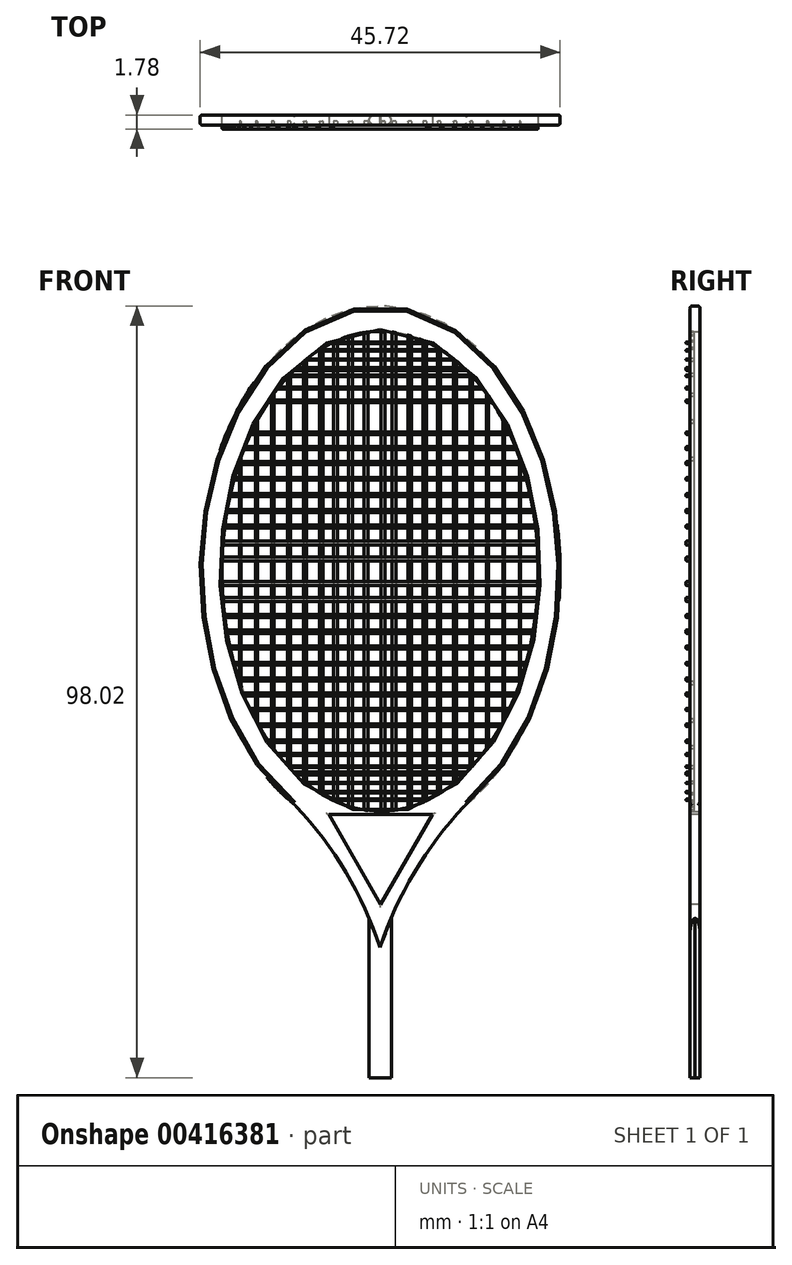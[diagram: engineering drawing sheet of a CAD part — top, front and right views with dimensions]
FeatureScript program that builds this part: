
annotation { "Feature Type Name" : "Feature", "Feature Type Description" : "" }
export const myFeature = defineFeature(function(context is Context, id is Id, definition is map)
    precondition{}
    {
        {
            var Q0;
            Q0=qCreatedBy(makeId("Front.planeOp"),FACE);
            var sketch = newSketch(context, id + "F0", { "sketchPlane" : qUnion([Q0])});
            skEllipse(sketch, "E0", {"center": v(0, 0) * mm, "majorRadius": 33.69 * mm, "minorRadius": 22.86 * mm, "majorAxis": v(0, 1)});
            skEllipse(sketch, "E1", {"center": v(0, 0) * mm, "majorRadius": 30.48 * mm, "minorRadius": 20.09 * mm, "majorAxis": v(0, 1)});
            skArc(sketch, "E2", {"start": v(13.9, -26.75) * mm, "mid": v(5.55, -36.34) * mm, "end": v(0, -47.78) * mm});
            skArc(sketch, "E3.MirrorCS", {"start": v(-13.9, -26.75) * mm, "mid": v(-5.55, -36.34) * mm, "end": v(0, -47.78) * mm});
            skSolve(sketch);
        }
        {
            var Q0;
            Q0 = qSketchRegion(id + "F0", true);
            extrude(context, id + "F1", {"entities" : qUnion([Q0]), "depth" : 1.27 * mm});
        }
        {
            var Q0;
            Q0=makeQuery(id+"F1.opExtrude","CAP_FACE",FACE,{"disambiguationData":[OSD([sQuery(id+"F0.wireOp",EDGE,"E0"),sQuery(id+"F0.wireOp",EDGE,"E1"),sQuery(id+"F0.wireOp",EDGE,"E2"),sQuery(id+"F0.wireOp",EDGE,"E3.MirrorCS")])],"isStart":false});
            var sketch = newSketch(context, id + "F2", { "sketchPlane" : qUnion([Q0])});
            skLineSegment(sketch, "E4", {"start": v(-6.5, -30.9) * mm, "end": v(6.64, -30.9) * mm});
            skLineSegment(sketch, "E5", {"start": v(6.64, -30.9) * mm, "end": v(0.07, -42.3) * mm});
            skLineSegment(sketch, "E6", {"start": v(0.07, -42.3) * mm, "end": v(-6.5, -30.9) * mm});
            skSolve(sketch);
        }
        {
            var Q0;
            Q0=makeQuery(id+"F2.imprint","IMPRINT",FACE,{"disambiguationData":[TD([[makeQuery(id+"F2.imprint","IMPRINT",EDGE,{"derivedFrom":sQuery(id+"F2.wireOp",EDGE,"E4")}),-1.0]])]});
            extrude(context, id + "F3", {"entities" : qUnion([Q0]), "operationType" : NewBodyOperationType.REMOVE, "oppositeDirection" : true, "depth" : 25.4 * mm});
        }
        {
            var Q0;
            Q0=qCreatedBy(makeId("Front.planeOp"),FACE);
            var sketch = newSketch(context, id + "F4", { "sketchPlane" : qUnion([Q0])});
            skLineSegment(sketch, "E7", {"start": v(1.42, -44.01) * mm, "end": v(1.42, -64.33) * mm});
            skLineSegment(sketch, "E8", {"start": v(1.42, -64.33) * mm, "end": v(-1.43, -64.33) * mm});
            skLineSegment(sketch, "E9", {"start": v(-1.43, -64.33) * mm, "end": v(-1.43, -44.01) * mm});
            skLineSegment(sketch, "E10", {"start": v(1.42, -44.01) * mm, "end": v(0, -47.74) * mm});
            skLineSegment(sketch, "E11", {"start": v(0, -47.74) * mm, "end": v(-1.43, -44.01) * mm});
            skSolve(sketch);
        }
        {
            var Q0;
            Q0 = qSketchRegion(id + "F4", true);
            extrude(context, id + "F5", {"entities" : qUnion([Q0]), "depth" : 1.27 * mm});
        }
        {
            var Q0;
            Q0=makeQuery(id+"F1.opExtrude","CAP_FACE",FACE,{"disambiguationData":[OSD([sQuery(id+"F0.wireOp",EDGE,"E0"),sQuery(id+"F0.wireOp",EDGE,"E1"),sQuery(id+"F0.wireOp",EDGE,"E2"),sQuery(id+"F0.wireOp",EDGE,"E3.MirrorCS")])],"isStart":false});
            var sketch = newSketch(context, id + "F6", { "sketchPlane" : qUnion([Q0])});
            skLineSegment(sketch, "E12", {"start": v(-15.82, 18.79) * mm, "end": v(-15.82, -18.79) * mm});
            skLineSegment(sketch, "E13", {"start": v(-13.79, 22.17) * mm, "end": v(-13.79, -22.17) * mm});
            skLineSegment(sketch, "E14", {"start": v(-11.75, 24.72) * mm, "end": v(-11.75, -24.72) * mm});
            skLineSegment(sketch, "E15", {"start": v(-9.72, 26.67) * mm, "end": v(-9.72, -26.67) * mm});
            skLineSegment(sketch, "E16", {"start": v(-7.69, 28.16) * mm, "end": v(-7.69, -28.16) * mm});
            skLineSegment(sketch, "E17.MirrorCS", {"start": v(7.69, 28.16) * mm, "end": v(7.69, -28.16) * mm});
            skLineSegment(sketch, "E18.MirrorCS", {"start": v(9.72, 26.67) * mm, "end": v(9.72, -26.67) * mm});
            skLineSegment(sketch, "E19.MirrorCS", {"start": v(11.75, 24.72) * mm, "end": v(11.75, -24.72) * mm});
            skLineSegment(sketch, "E20.MirrorCS", {"start": v(13.79, 22.17) * mm, "end": v(13.79, -22.17) * mm});
            skLineSegment(sketch, "E21.MirrorCS", {"start": v(15.82, 18.79) * mm, "end": v(15.82, -18.79) * mm});
            skLineSegment(sketch, "E22", {"start": v(-17.85, 13.98) * mm, "end": v(-17.85, -13.98) * mm});
            skLineSegment(sketch, "E23.MirrorCS", {"start": v(17.85, 13.98) * mm, "end": v(17.85, -13.98) * mm});
            skLineSegment(sketch, "E24", {"start": v(-5.9, 29.13) * mm, "end": v(-5.9, -29.13) * mm});
            skLineSegment(sketch, "E25", {"start": v(-4.01, 29.87) * mm, "end": v(-4.01, -29.87) * mm});
            skLineSegment(sketch, "E26", {"start": v(-2.03, 30.32) * mm, "end": v(-2.03, -30.32) * mm});
            skLineSegment(sketch, "E27.MirrorCS", {"start": v(2.03, 30.32) * mm, "end": v(2.03, -30.32) * mm});
            skLineSegment(sketch, "E28.MirrorCS", {"start": v(4.01, 29.87) * mm, "end": v(4.01, -29.87) * mm});
            skLineSegment(sketch, "E29.MirrorCS", {"start": v(5.9, 29.13) * mm, "end": v(5.9, -29.13) * mm});
            skLineSegment(sketch, "E30", {"start": v(-17.68, 14.46) * mm, "end": v(-17.68, -14.46) * mm});
            skLineSegment(sketch, "E31", {"start": v(-15.58, 19.24) * mm, "end": v(-15.58, -19.24) * mm});
            skLineSegment(sketch, "E32", {"start": v(-13.5, 22.58) * mm, "end": v(-13.5, -22.58) * mm});
            skLineSegment(sketch, "E33", {"start": v(-11.4, 25.09) * mm, "end": v(-11.4, -25.09) * mm});
            skLineSegment(sketch, "E34", {"start": v(-9.33, 27) * mm, "end": v(-9.33, -27) * mm});
            skLineSegment(sketch, "E35", {"start": v(-7.26, 28.42) * mm, "end": v(-7.26, -28.42) * mm});
            skLineSegment(sketch, "E36", {"start": v(-5.44, 29.34) * mm, "end": v(-5.44, -29.34) * mm});
            skLineSegment(sketch, "E37", {"start": v(-3.52, 30) * mm, "end": v(-3.52, -30) * mm});
            skLineSegment(sketch, "E38", {"start": v(-1.53, 30.4) * mm, "end": v(-1.53, -30.4) * mm});
            skLineSegment(sketch, "E39.MirrorCS", {"start": v(17.68, 14.46) * mm, "end": v(17.68, -14.46) * mm});
            skLineSegment(sketch, "E40.MirrorCS", {"start": v(15.58, 19.24) * mm, "end": v(15.58, -19.24) * mm});
            skLineSegment(sketch, "E41.MirrorCS", {"start": v(13.5, 22.58) * mm, "end": v(13.5, -22.58) * mm});
            skLineSegment(sketch, "E42.MirrorCS", {"start": v(11.4, 25.09) * mm, "end": v(11.4, -25.09) * mm});
            skLineSegment(sketch, "E43.MirrorCS", {"start": v(9.33, 27) * mm, "end": v(9.33, -27) * mm});
            skLineSegment(sketch, "E44.MirrorCS", {"start": v(7.26, 28.42) * mm, "end": v(7.26, -28.42) * mm});
            skLineSegment(sketch, "E45.MirrorCS", {"start": v(5.44, 29.34) * mm, "end": v(5.44, -29.34) * mm});
            skLineSegment(sketch, "E46.MirrorCS", {"start": v(3.52, 30) * mm, "end": v(3.52, -30) * mm});
            skLineSegment(sketch, "E47.MirrorCS", {"start": v(1.53, 30.4) * mm, "end": v(1.53, -30.4) * mm});
            skLineSegment(sketch, "E48", {"start": v(0.1, 30.48) * mm, "end": v(0.1, -30.48) * mm});
            skLineSegment(sketch, "E49", {"start": v(0.61, 30.47) * mm, "end": v(0.61, -30.47) * mm});
            skSolve(sketch);
        }
        {
            var Q0;
            Q0=makeQuery(id+"F6.imprint","IMPRINT",FACE,{"disambiguationData":[TD([[makeQuery(id+"F6.imprint","IMPRINT",EDGE,{"derivedFrom":makeQuery(id+"F1.opExtrude","CAP_EDGE",EDGE,{"disambiguationData":[OSD([sQuery(id+"F0.wireOp",EDGE,"E0")])],"isStart":false})}),1.0]])]});
            var sketch = newSketch(context, id + "F7", { "sketchPlane" : qUnion([Q0])});
            skLineSegment(sketch, "E50", {"start": v(-5.9, 29.13) * mm, "end": v(5.9, 29.13) * mm});
            skLineSegment(sketch, "E51", {"start": v(-7.69, 28.16) * mm, "end": v(7.69, 28.16) * mm});
            skLineSegment(sketch, "E52", {"start": v(-9.35, 26.98) * mm, "end": v(9.35, 26.98) * mm});
            skLineSegment(sketch, "E53", {"start": v(-11.54, 24.95) * mm, "end": v(11.54, 24.95) * mm});
            skLineSegment(sketch, "E54", {"start": v(-12.87, 23.4) * mm, "end": v(12.87, 23.4) * mm});
            skLineSegment(sketch, "E55", {"start": v(-14.06, 21.77) * mm, "end": v(14.06, 21.77) * mm});
            skLineSegment(sketch, "E56", {"start": v(-15.3, 19.73) * mm, "end": v(15.3, 19.73) * mm});
            skLineSegment(sketch, "E57", {"start": v(15.3, 19.73) * mm, "end": v(-15.3, 19.73) * mm});
            skLineSegment(sketch, "E58", {"start": v(-16.35, 17.7) * mm, "end": v(16.35, 17.7) * mm});
            skLineSegment(sketch, "E59", {"start": v(-17.16, 15.84) * mm, "end": v(17.16, 15.84) * mm});
            skLineSegment(sketch, "E60", {"start": v(-17.87, 13.93) * mm, "end": v(17.87, 13.93) * mm});
            skLineSegment(sketch, "E61", {"start": v(-18.5, 11.9) * mm, "end": v(18.5, 11.9) * mm});
            skLineSegment(sketch, "E62", {"start": v(-19, 9.87) * mm, "end": v(19, 9.87) * mm});
            skLineSegment(sketch, "E63", {"start": v(-19.4, 7.88) * mm, "end": v(19.4, 7.88) * mm});
            skLineSegment(sketch, "E64", {"start": v(-19.71, 5.87) * mm, "end": v(19.71, 5.87) * mm});
            skLineSegment(sketch, "E65", {"start": v(-20.05, 3.83) * mm, "end": v(19.93, 3.83) * mm});
            skLineSegment(sketch, "E66", {"start": v(-20.05, 1.8) * mm, "end": v(20.05, 1.8) * mm});
            skLineSegment(sketch, "E67", {"start": v(-20.99, 0) * mm, "end": v(20.09, 0) * mm});
            skLineSegment(sketch, "E68.MirrorCS", {"start": v(-20.05, -1.8) * mm, "end": v(20.05, -1.8) * mm});
            skLineSegment(sketch, "E69.MirrorCS", {"start": v(-20.05, -3.83) * mm, "end": v(19.93, -3.83) * mm});
            skLineSegment(sketch, "E70.MirrorCS", {"start": v(-19.71, -5.87) * mm, "end": v(19.71, -5.87) * mm});
            skLineSegment(sketch, "E71.MirrorCS", {"start": v(-19.4, -7.88) * mm, "end": v(19.4, -7.88) * mm});
            skLineSegment(sketch, "E72.MirrorCS", {"start": v(-5.9, -29.13) * mm, "end": v(5.9, -29.13) * mm});
            skLineSegment(sketch, "E73.MirrorCS", {"start": v(-7.69, -28.16) * mm, "end": v(7.69, -28.16) * mm});
            skLineSegment(sketch, "E74.MirrorCS", {"start": v(-9.35, -26.98) * mm, "end": v(9.35, -26.98) * mm});
            skLineSegment(sketch, "E75.MirrorCS", {"start": v(-11.54, -24.95) * mm, "end": v(11.54, -24.95) * mm});
            skLineSegment(sketch, "E76.MirrorCS", {"start": v(-12.87, -23.4) * mm, "end": v(12.87, -23.4) * mm});
            skLineSegment(sketch, "E77.MirrorCS", {"start": v(-14.06, -21.77) * mm, "end": v(14.06, -21.77) * mm});
            skLineSegment(sketch, "E78.MirrorCS", {"start": v(15.3, -19.73) * mm, "end": v(-15.3, -19.73) * mm});
            skLineSegment(sketch, "E79.MirrorCS", {"start": v(-16.35, -17.7) * mm, "end": v(16.35, -17.7) * mm});
            skLineSegment(sketch, "E80.MirrorCS", {"start": v(-17.16, -15.84) * mm, "end": v(17.16, -15.84) * mm});
            skLineSegment(sketch, "E81.MirrorCS", {"start": v(-17.87, -13.93) * mm, "end": v(17.87, -13.93) * mm});
            skLineSegment(sketch, "E82.MirrorCS", {"start": v(-18.5, -11.9) * mm, "end": v(18.5, -11.9) * mm});
            skLineSegment(sketch, "E83.MirrorCS", {"start": v(-19, -9.87) * mm, "end": v(19, -9.87) * mm});
            skLineSegment(sketch, "E84", {"start": v(-6.37, 28.93) * mm, "end": v(7.07, 28.93) * mm});
            skLineSegment(sketch, "E85", {"start": v(-8.16, 27.96) * mm, "end": v(8.72, 27.96) * mm});
            skLineSegment(sketch, "E86", {"start": v(-9.83, 26.82) * mm, "end": v(10.64, 26.82) * mm});
            skLineSegment(sketch, "E87", {"start": v(-11.99, 24.7) * mm, "end": v(12.2, 24.7) * mm});
            skLineSegment(sketch, "E88", {"start": v(-13.3, 23.14) * mm, "end": v(13.48, 23.14) * mm});
            skLineSegment(sketch, "E89", {"start": v(-14.45, 21.44) * mm, "end": v(14.63, 21.44) * mm});
            skLineSegment(sketch, "E90", {"start": v(-15.67, 19.37) * mm, "end": v(15.85, 19.37) * mm});
            skLineSegment(sketch, "E91", {"start": v(-17.16, 17.4) * mm, "end": v(16.88, 17.4) * mm});
            skLineSegment(sketch, "E92", {"start": v(-17.47, 15.44) * mm, "end": v(17.92, 15.44) * mm});
            skLineSegment(sketch, "E93", {"start": v(-18.2, 13.54) * mm, "end": v(18.63, 13.54) * mm});
            skLineSegment(sketch, "E94", {"start": v(-18.88, 11.57) * mm, "end": v(19.66, 11.57) * mm});
            skLineSegment(sketch, "E95", {"start": v(-19.35, 9.5) * mm, "end": v(19.83, 9.5) * mm});
            skLineSegment(sketch, "E96", {"start": v(-19.66, 7.44) * mm, "end": v(19.96, 7.44) * mm});
            skLineSegment(sketch, "E97", {"start": v(-20.08, 5.51) * mm, "end": v(19.86, 5.51) * mm});
            skLineSegment(sketch, "E98", {"start": v(-20.08, 3.33) * mm, "end": v(20.38, 3.33) * mm});
            skLineSegment(sketch, "E99", {"start": v(-20.2, 1.32) * mm, "end": v(20.18, 1.32) * mm});
            skLineSegment(sketch, "E100.MirrorCS", {"start": v(-20.2, -1.32) * mm, "end": v(20.18, -1.32) * mm});
            skLineSegment(sketch, "E101.MirrorCS", {"start": v(-20.08, -3.33) * mm, "end": v(20.38, -3.33) * mm});
            skLineSegment(sketch, "E102.MirrorCS", {"start": v(-20.08, -5.51) * mm, "end": v(19.86, -5.51) * mm});
            skLineSegment(sketch, "E103.MirrorCS", {"start": v(-19.66, -7.44) * mm, "end": v(19.96, -7.44) * mm});
            skLineSegment(sketch, "E104.MirrorCS", {"start": v(-19.35, -9.5) * mm, "end": v(19.83, -9.5) * mm});
            skLineSegment(sketch, "E105.MirrorCS", {"start": v(-18.88, -11.57) * mm, "end": v(19.66, -11.57) * mm});
            skLineSegment(sketch, "E106.MirrorCS", {"start": v(-18.2, -13.54) * mm, "end": v(18.63, -13.54) * mm});
            skLineSegment(sketch, "E107.MirrorCS", {"start": v(-17.47, -15.44) * mm, "end": v(17.92, -15.44) * mm});
            skLineSegment(sketch, "E108.MirrorCS", {"start": v(-17.16, -17.4) * mm, "end": v(16.88, -17.4) * mm});
            skLineSegment(sketch, "E109.MirrorCS", {"start": v(-15.67, -19.37) * mm, "end": v(15.85, -19.37) * mm});
            skLineSegment(sketch, "E110.MirrorCS", {"start": v(-14.45, -21.44) * mm, "end": v(14.63, -21.44) * mm});
            skLineSegment(sketch, "E111.MirrorCS", {"start": v(-13.3, -23.14) * mm, "end": v(13.48, -23.14) * mm});
            skLineSegment(sketch, "E112.MirrorCS", {"start": v(-11.99, -24.7) * mm, "end": v(12.2, -24.7) * mm});
            skLineSegment(sketch, "E113.MirrorCS", {"start": v(-9.83, -26.82) * mm, "end": v(10.64, -26.82) * mm});
            skLineSegment(sketch, "E114.MirrorCS", {"start": v(-8.16, -27.96) * mm, "end": v(8.72, -27.96) * mm});
            skLineSegment(sketch, "E115.MirrorCS", {"start": v(-6.37, -28.93) * mm, "end": v(7.07, -28.93) * mm});
            skLineSegment(sketch, "E116", {"start": v(-11.06, 25.88) * mm, "end": v(10.6, 25.88) * mm});
            skLineSegment(sketch, "E117", {"start": v(-11.42, 25.52) * mm, "end": v(10.98, 25.52) * mm});
            skLineSegment(sketch, "E118.MirrorCS", {"start": v(-11.06, -25.88) * mm, "end": v(10.6, -25.88) * mm});
            skLineSegment(sketch, "E119.MirrorCS", {"start": v(-11.42, -25.52) * mm, "end": v(10.98, -25.52) * mm});
            skSolve(sketch);
        }
        {
            var Q0;
            Q0=makeQuery(id+"F5.opExtrude","CAP_EDGE",EDGE,{"disambiguationData":[OSD([sQuery(id+"F4.wireOp",EDGE,"E7")])],"isStart":true});
            var Q1;
            Q1=makeQuery(id+"F5.opExtrude","CAP_EDGE",EDGE,{"disambiguationData":[OSD([sQuery(id+"F4.wireOp",EDGE,"E7")])],"isStart":false});
            var Q2;
            Q2=makeQuery(id+"F5.opExtrude","CAP_EDGE",EDGE,{"disambiguationData":[OSD([sQuery(id+"F4.wireOp",EDGE,"E9")])],"isStart":true});
            var Q3;
            Q3=makeQuery(id+"F5.opExtrude","CAP_EDGE",EDGE,{"disambiguationData":[OSD([sQuery(id+"F4.wireOp",EDGE,"E9")])],"isStart":false});
            fillet(context, id + "F8", {"entities" : qUnion([Q0, Q1, Q2, Q3]), "radius" : 0.76 * mm, "tangentPropagation" : true, "allowEdgeOverflow" : false});
        }
        {
            var Q0;
            {var subQ0=sQuery(id+"F6.wireOp",EDGE,"E22");Q0=makeQuery(id+"F6.imprint","IMPRINT",FACE,{"disambiguationData":[TD([[makeQuery(id+"F6.imprint","IMPRINT",EDGE,{"derivedFrom":subQ0}),1.0]])]});}
            var Q1;
            {var subQ0=sQuery(id+"F6.wireOp",EDGE,"E12");Q1=makeQuery(id+"F6.imprint","IMPRINT",FACE,{"disambiguationData":[TD([[makeQuery(id+"F6.imprint","IMPRINT",EDGE,{"derivedFrom":subQ0}),1.0]])]});}
            var Q2;
            {var subQ0=sQuery(id+"F6.wireOp",EDGE,"E13");Q2=makeQuery(id+"F6.imprint","IMPRINT",FACE,{"disambiguationData":[TD([[makeQuery(id+"F6.imprint","IMPRINT",EDGE,{"derivedFrom":subQ0}),1.0]])]});}
            var Q3;
            {var subQ0=sQuery(id+"F6.wireOp",EDGE,"E14");Q3=makeQuery(id+"F6.imprint","IMPRINT",FACE,{"disambiguationData":[TD([[makeQuery(id+"F6.imprint","IMPRINT",EDGE,{"derivedFrom":subQ0}),1.0]])]});}
            var Q4;
            {var subQ0=sQuery(id+"F6.wireOp",EDGE,"E16");Q4=makeQuery(id+"F6.imprint","IMPRINT",FACE,{"disambiguationData":[TD([[makeQuery(id+"F6.imprint","IMPRINT",EDGE,{"derivedFrom":subQ0}),1.0]])]});}
            var Q5;
            {var subQ0=sQuery(id+"F6.wireOp",EDGE,"E25");Q5=makeQuery(id+"F6.imprint","IMPRINT",FACE,{"disambiguationData":[TD([[makeQuery(id+"F6.imprint","IMPRINT",EDGE,{"derivedFrom":subQ0}),1.0]])]});}
            var Q6;
            {var subQ0=sQuery(id+"F6.wireOp",EDGE,"E24");Q6=makeQuery(id+"F6.imprint","IMPRINT",FACE,{"disambiguationData":[TD([[makeQuery(id+"F6.imprint","IMPRINT",EDGE,{"derivedFrom":subQ0}),1.0]])]});}
            var Q7;
            {var subQ0=sQuery(id+"F6.wireOp",EDGE,"E15");Q7=makeQuery(id+"F6.imprint","IMPRINT",FACE,{"disambiguationData":[TD([[makeQuery(id+"F6.imprint","IMPRINT",EDGE,{"derivedFrom":subQ0}),1.0]])]});}
            var Q8;
            {var subQ0=sQuery(id+"F6.wireOp",EDGE,"E26");Q8=makeQuery(id+"F6.imprint","IMPRINT",FACE,{"disambiguationData":[TD([[makeQuery(id+"F6.imprint","IMPRINT",EDGE,{"derivedFrom":subQ0}),1.0]])]});}
            var Q9;
            {var subQ0=sQuery(id+"F6.wireOp",EDGE,"E27.MirrorCS");Q9=makeQuery(id+"F6.imprint","IMPRINT",FACE,{"disambiguationData":[TD([[makeQuery(id+"F6.imprint","IMPRINT",EDGE,{"derivedFrom":subQ0}),-1.0]])]});}
            var Q10;
            {var subQ0=sQuery(id+"F6.wireOp",EDGE,"E23.MirrorCS");Q10=makeQuery(id+"F6.imprint","IMPRINT",FACE,{"disambiguationData":[TD([[makeQuery(id+"F6.imprint","IMPRINT",EDGE,{"derivedFrom":subQ0}),-1.0]])]});}
            var Q11;
            {var subQ0=sQuery(id+"F6.wireOp",EDGE,"E18.MirrorCS");Q11=makeQuery(id+"F6.imprint","IMPRINT",FACE,{"disambiguationData":[TD([[makeQuery(id+"F6.imprint","IMPRINT",EDGE,{"derivedFrom":subQ0}),-1.0]])]});}
            var Q12;
            {var subQ0=sQuery(id+"F6.wireOp",EDGE,"E29.MirrorCS");Q12=makeQuery(id+"F6.imprint","IMPRINT",FACE,{"disambiguationData":[TD([[makeQuery(id+"F6.imprint","IMPRINT",EDGE,{"derivedFrom":subQ0}),-1.0]])]});}
            var Q13;
            {var subQ0=sQuery(id+"F6.wireOp",EDGE,"E17.MirrorCS");Q13=makeQuery(id+"F6.imprint","IMPRINT",FACE,{"disambiguationData":[TD([[makeQuery(id+"F6.imprint","IMPRINT",EDGE,{"derivedFrom":subQ0}),-1.0]])]});}
            var Q14;
            {var subQ0=sQuery(id+"F6.wireOp",EDGE,"E19.MirrorCS");Q14=makeQuery(id+"F6.imprint","IMPRINT",FACE,{"disambiguationData":[TD([[makeQuery(id+"F6.imprint","IMPRINT",EDGE,{"derivedFrom":subQ0}),-1.0]])]});}
            var Q15;
            {var subQ0=sQuery(id+"F6.wireOp",EDGE,"E20.MirrorCS");Q15=makeQuery(id+"F6.imprint","IMPRINT",FACE,{"disambiguationData":[TD([[makeQuery(id+"F6.imprint","IMPRINT",EDGE,{"derivedFrom":subQ0}),-1.0]])]});}
            var Q16;
            {var subQ0=sQuery(id+"F6.wireOp",EDGE,"E21.MirrorCS");Q16=makeQuery(id+"F6.imprint","IMPRINT",FACE,{"disambiguationData":[TD([[makeQuery(id+"F6.imprint","IMPRINT",EDGE,{"derivedFrom":subQ0}),-1.0]])]});}
            var Q17;
            {var subQ0=sQuery(id+"F6.wireOp",EDGE,"E28.MirrorCS");Q17=makeQuery(id+"F6.imprint","IMPRINT",FACE,{"disambiguationData":[TD([[makeQuery(id+"F6.imprint","IMPRINT",EDGE,{"derivedFrom":subQ0}),-1.0]])]});}
            var Q18;
            {var subQ0=sQuery(id+"F6.wireOp",EDGE,"E48");Q18=makeQuery(id+"F6.imprint","IMPRINT",FACE,{"disambiguationData":[TD([[makeQuery(id+"F6.imprint","IMPRINT",EDGE,{"derivedFrom":subQ0}),1.0]])]});}
            extrude(context, id + "F9", {"entities" : qUnion([Q0, Q1, Q2, Q3, Q4, Q5, Q6, Q7, Q8, Q9, Q10, Q11, Q12, Q13, Q14, Q15, Q16, Q17, Q18]), "oppositeDirection" : true, "depth" : 0.5 * mm});
        }
        {
            var Q0;
            {var subQ0=sQuery(id+"F7.wireOp",EDGE,"E59");Q0=makeQuery(id+"F7.imprint","IMPRINT",FACE,{"disambiguationData":[TD([[makeQuery(id+"F7.imprint","IMPRINT",EDGE,{"derivedFrom":subQ0}),-1.0]])]});}
            var Q1;
            {var subQ0=sQuery(id+"F7.wireOp",EDGE,"E58");Q1=makeQuery(id+"F7.imprint","IMPRINT",FACE,{"disambiguationData":[TD([[makeQuery(id+"F7.imprint","IMPRINT",EDGE,{"derivedFrom":subQ0}),-1.0]])]});}
            var Q2;
            {var subQ0=sQuery(id+"F7.wireOp",EDGE,"E60");Q2=makeQuery(id+"F7.imprint","IMPRINT",FACE,{"disambiguationData":[TD([[makeQuery(id+"F7.imprint","IMPRINT",EDGE,{"derivedFrom":subQ0}),-1.0]])]});}
            var Q3;
            {var subQ0=sQuery(id+"F7.wireOp",EDGE,"E61");Q3=makeQuery(id+"F7.imprint","IMPRINT",FACE,{"disambiguationData":[TD([[makeQuery(id+"F7.imprint","IMPRINT",EDGE,{"derivedFrom":subQ0}),-1.0]])]});}
            var Q4;
            {var subQ0=sQuery(id+"F7.wireOp",EDGE,"E79.MirrorCS");Q4=makeQuery(id+"F7.imprint","IMPRINT",FACE,{"disambiguationData":[TD([[makeQuery(id+"F7.imprint","IMPRINT",EDGE,{"derivedFrom":subQ0}),1.0]])]});}
            var Q5;
            {var subQ0=sQuery(id+"F7.wireOp",EDGE,"E80.MirrorCS");Q5=makeQuery(id+"F7.imprint","IMPRINT",FACE,{"disambiguationData":[TD([[makeQuery(id+"F7.imprint","IMPRINT",EDGE,{"derivedFrom":subQ0}),1.0]])]});}
            var Q6;
            {var subQ0=sQuery(id+"F7.wireOp",EDGE,"E81.MirrorCS");Q6=makeQuery(id+"F7.imprint","IMPRINT",FACE,{"disambiguationData":[TD([[makeQuery(id+"F7.imprint","IMPRINT",EDGE,{"derivedFrom":subQ0}),1.0]])]});}
            var Q7;
            {var subQ0=sQuery(id+"F7.wireOp",EDGE,"E82.MirrorCS");Q7=makeQuery(id+"F7.imprint","IMPRINT",FACE,{"disambiguationData":[TD([[makeQuery(id+"F7.imprint","IMPRINT",EDGE,{"derivedFrom":subQ0}),1.0]])]});}
            var Q8;
            {var subQ0=sQuery(id+"F7.wireOp",EDGE,"E70.MirrorCS");Q8=makeQuery(id+"F7.imprint","IMPRINT",FACE,{"disambiguationData":[TD([[makeQuery(id+"F7.imprint","IMPRINT",EDGE,{"derivedFrom":subQ0}),1.0]])]});}
            var Q9;
            {var subQ0=sQuery(id+"F7.wireOp",EDGE,"E64");Q9=makeQuery(id+"F7.imprint","IMPRINT",FACE,{"disambiguationData":[TD([[makeQuery(id+"F7.imprint","IMPRINT",EDGE,{"derivedFrom":subQ0}),-1.0]])]});}
            var Q10;
            {var subQ0=sQuery(id+"F7.wireOp",EDGE,"E69.MirrorCS");var subQ1=sQuery(id+"F6.wireOp",EDGE,"E23.MirrorCS");var subQ2=makeQuery(id+"F1.opExtrude","CAP_EDGE",EDGE,{"disambiguationData":[OSD([sQuery(id+"F0.wireOp",EDGE,"E1")])],"isStart":false});var subQ3=makeQuery(id+"F6.imprint","IMPRINT",EDGE,{"disambiguationData":[TD([[makeQuery(id+"F6.imprint","INTERSECT",VERTEX,{"disambiguationData":[OD(0.0)],"derivedFrom":[subQ2,subQ1]}),1.0]])],"derivedFrom":subQ2});var subQ4=makeQuery(id+"F7.imprint","INTERSECT",VERTEX,{"derivedFrom":[subQ3,subQ0]});Q10=makeQuery(id+"F7.imprint","IMPRINT",FACE,{"disambiguationData":[TD([[makeQuery(id+"F7.imprint","IMPRINT",EDGE,{"disambiguationData":[TD([[subQ4,1.0]])],"derivedFrom":subQ0}),1.0]])]});}
            var Q11;
            {var subQ0=sQuery(id+"F7.wireOp",EDGE,"E77.MirrorCS");Q11=makeQuery(id+"F7.imprint","IMPRINT",FACE,{"disambiguationData":[TD([[makeQuery(id+"F7.imprint","IMPRINT",EDGE,{"derivedFrom":subQ0}),1.0]])]});}
            var Q12;
            {var subQ0=sQuery(id+"F7.wireOp",EDGE,"E72.MirrorCS");Q12=makeQuery(id+"F7.imprint","IMPRINT",FACE,{"disambiguationData":[TD([[makeQuery(id+"F7.imprint","IMPRINT",EDGE,{"derivedFrom":subQ0}),1.0]])]});}
            var Q13;
            {var subQ5=sQuery(id+"F7.wireOp",EDGE,"E53");Q13=makeQuery(id+"F7.imprint","IMPRINT",FACE,{"disambiguationData":[TD([[makeQuery(id+"F7.imprint","IMPRINT",EDGE,{"derivedFrom":subQ5}),-1.0]])]});}
            var Q14;
            {var subQ0=sQuery(id+"F7.wireOp",EDGE,"E55");Q14=makeQuery(id+"F7.imprint","IMPRINT",FACE,{"disambiguationData":[TD([[makeQuery(id+"F7.imprint","IMPRINT",EDGE,{"derivedFrom":subQ0}),-1.0]])]});}
            var Q15;
            {var subQ0=sQuery(id+"F7.wireOp",EDGE,"E54");Q15=makeQuery(id+"F7.imprint","IMPRINT",FACE,{"disambiguationData":[TD([[makeQuery(id+"F7.imprint","IMPRINT",EDGE,{"derivedFrom":subQ0}),-1.0]])]});}
            var Q16;
            {var subQ0=sQuery(id+"F7.wireOp",EDGE,"E57");Q16=makeQuery(id+"F7.imprint","IMPRINT",FACE,{"disambiguationData":[TD([[makeQuery(id+"F7.imprint","IMPRINT",EDGE,{"derivedFrom":subQ0}),1.0]])]});}
            var Q17;
            {var subQ0=sQuery(id+"F7.wireOp",EDGE,"E52");Q17=makeQuery(id+"F7.imprint","IMPRINT",FACE,{"disambiguationData":[TD([[makeQuery(id+"F7.imprint","IMPRINT",EDGE,{"derivedFrom":subQ0}),-1.0]])]});}
            var Q18;
            {var subQ0=sQuery(id+"F7.wireOp",EDGE,"E51");Q18=makeQuery(id+"F7.imprint","IMPRINT",FACE,{"disambiguationData":[TD([[makeQuery(id+"F7.imprint","IMPRINT",EDGE,{"derivedFrom":subQ0}),-1.0]])]});}
            var Q19;
            {var subQ0=sQuery(id+"F7.wireOp",EDGE,"E50");Q19=makeQuery(id+"F7.imprint","IMPRINT",FACE,{"disambiguationData":[TD([[makeQuery(id+"F7.imprint","IMPRINT",EDGE,{"derivedFrom":subQ0}),-1.0]])]});}
            var Q20;
            {var subQ0=sQuery(id+"F7.wireOp",EDGE,"E71.MirrorCS");Q20=makeQuery(id+"F7.imprint","IMPRINT",FACE,{"disambiguationData":[TD([[makeQuery(id+"F7.imprint","IMPRINT",EDGE,{"derivedFrom":subQ0}),1.0]])]});}
            var Q21;
            {var subQ0=sQuery(id+"F7.wireOp",EDGE,"E83.MirrorCS");Q21=makeQuery(id+"F7.imprint","IMPRINT",FACE,{"disambiguationData":[TD([[makeQuery(id+"F7.imprint","IMPRINT",EDGE,{"derivedFrom":subQ0}),1.0]])]});}
            var Q22;
            {var subQ0=sQuery(id+"F7.wireOp",EDGE,"E65");var subQ1=sQuery(id+"F6.wireOp",EDGE,"E23.MirrorCS");var subQ2=makeQuery(id+"F1.opExtrude","CAP_EDGE",EDGE,{"disambiguationData":[OSD([sQuery(id+"F0.wireOp",EDGE,"E1")])],"isStart":false});var subQ3=makeQuery(id+"F6.imprint","IMPRINT",EDGE,{"disambiguationData":[TD([[makeQuery(id+"F6.imprint","INTERSECT",VERTEX,{"disambiguationData":[OD(0.0)],"derivedFrom":[subQ2,subQ1]}),1.0]])],"derivedFrom":subQ2});var subQ4=makeQuery(id+"F7.imprint","INTERSECT",VERTEX,{"derivedFrom":[subQ3,subQ0]});Q22=makeQuery(id+"F7.imprint","IMPRINT",FACE,{"disambiguationData":[TD([[makeQuery(id+"F7.imprint","IMPRINT",EDGE,{"disambiguationData":[TD([[subQ4,1.0]])],"derivedFrom":subQ0}),-1.0]])]});}
            var Q23;
            {var subQ0=sQuery(id+"F7.wireOp",EDGE,"E66");Q23=makeQuery(id+"F7.imprint","IMPRINT",FACE,{"disambiguationData":[TD([[makeQuery(id+"F7.imprint","IMPRINT",EDGE,{"derivedFrom":subQ0}),-1.0]])]});}
            var Q24;
            {var subQ0=sQuery(id+"F7.wireOp",EDGE,"E76.MirrorCS");Q24=makeQuery(id+"F7.imprint","IMPRINT",FACE,{"disambiguationData":[TD([[makeQuery(id+"F7.imprint","IMPRINT",EDGE,{"derivedFrom":subQ0}),1.0]])]});}
            var Q25;
            {var subQ0=sQuery(id+"F7.wireOp",EDGE,"E73.MirrorCS");Q25=makeQuery(id+"F7.imprint","IMPRINT",FACE,{"disambiguationData":[TD([[makeQuery(id+"F7.imprint","IMPRINT",EDGE,{"derivedFrom":subQ0}),1.0]])]});}
            var Q26;
            {var subQ0=sQuery(id+"F7.wireOp",EDGE,"E63");Q26=makeQuery(id+"F7.imprint","IMPRINT",FACE,{"disambiguationData":[TD([[makeQuery(id+"F7.imprint","IMPRINT",EDGE,{"derivedFrom":subQ0}),-1.0]])]});}
            var Q27;
            {var subQ0=sQuery(id+"F7.wireOp",EDGE,"E62");Q27=makeQuery(id+"F7.imprint","IMPRINT",FACE,{"disambiguationData":[TD([[makeQuery(id+"F7.imprint","IMPRINT",EDGE,{"derivedFrom":subQ0}),-1.0]])]});}
            var Q28;
            {var subQ0=sQuery(id+"F7.wireOp",EDGE,"E68.MirrorCS");Q28=makeQuery(id+"F7.imprint","IMPRINT",FACE,{"disambiguationData":[TD([[makeQuery(id+"F7.imprint","IMPRINT",EDGE,{"derivedFrom":subQ0}),1.0]])]});}
            var Q29;
            {var subQ0=sQuery(id+"F7.wireOp",EDGE,"E78.MirrorCS");Q29=makeQuery(id+"F7.imprint","IMPRINT",FACE,{"disambiguationData":[TD([[makeQuery(id+"F7.imprint","IMPRINT",EDGE,{"derivedFrom":subQ0}),-1.0]])]});}
            var Q30;
            {var subQ0=sQuery(id+"F7.wireOp",EDGE,"E74.MirrorCS");Q30=makeQuery(id+"F7.imprint","IMPRINT",FACE,{"disambiguationData":[TD([[makeQuery(id+"F7.imprint","IMPRINT",EDGE,{"derivedFrom":subQ0}),1.0]])]});}
            var Q31;
            {var subQ5=sQuery(id+"F7.wireOp",EDGE,"E75.MirrorCS");Q31=makeQuery(id+"F7.imprint","IMPRINT",FACE,{"disambiguationData":[TD([[makeQuery(id+"F7.imprint","IMPRINT",EDGE,{"derivedFrom":subQ5}),1.0]])]});}
            var Q32;
            {var subQ0=sQuery(id+"F7.wireOp",EDGE,"E118.MirrorCS");var subQ1=makeQuery(id+"F1.opExtrude","CAP_EDGE",EDGE,{"disambiguationData":[OSD([sQuery(id+"F0.wireOp",EDGE,"E1")])],"isStart":false});var subQ2=makeQuery(id+"F6.imprint","IMPRINT",EDGE,{"disambiguationData":[TD([[makeQuery(id+"F6.imprint","INTERSECT",VERTEX,{"disambiguationData":[OD(1.0)],"derivedFrom":[subQ1,sQuery(id+"F6.wireOp",EDGE,"E18.MirrorCS")]}),-1.0]])],"derivedFrom":subQ1});var subQ3=makeQuery(id+"F7.imprint","INTERSECT",VERTEX,{"derivedFrom":[subQ2,subQ0]});Q32=makeQuery(id+"F7.imprint","IMPRINT",FACE,{"disambiguationData":[TD([[makeQuery(id+"F7.imprint","IMPRINT",EDGE,{"disambiguationData":[TD([[subQ3,1.0]])],"derivedFrom":subQ0}),1.0]])]});}
            var Q33;
            {var subQ0=sQuery(id+"F7.wireOp",EDGE,"E116");var subQ1=makeQuery(id+"F1.opExtrude","CAP_EDGE",EDGE,{"disambiguationData":[OSD([sQuery(id+"F0.wireOp",EDGE,"E1")])],"isStart":false});var subQ2=makeQuery(id+"F6.imprint","IMPRINT",EDGE,{"disambiguationData":[TD([[makeQuery(id+"F6.imprint","INTERSECT",VERTEX,{"disambiguationData":[OD(0.0)],"derivedFrom":[subQ1,sQuery(id+"F6.wireOp",EDGE,"E18.MirrorCS")]}),1.0]])],"derivedFrom":subQ1});var subQ3=makeQuery(id+"F7.imprint","INTERSECT",VERTEX,{"derivedFrom":[subQ2,subQ0]});Q33=makeQuery(id+"F7.imprint","IMPRINT",FACE,{"disambiguationData":[TD([[makeQuery(id+"F7.imprint","IMPRINT",EDGE,{"disambiguationData":[TD([[subQ3,1.0]])],"derivedFrom":subQ0}),-1.0]])]});}
            extrude(context, id + "F10", {"entities" : qUnion([Q0, Q1, Q2, Q3, Q4, Q5, Q6, Q7, Q8, Q9, Q10, Q11, Q12, Q13, Q14, Q15, Q16, Q17, Q18, Q19, Q20, Q21, Q22, Q23, Q24, Q25, Q26, Q27, Q28, Q29, Q30, Q31, Q32, Q33]), "depth" : 0.5 * mm});
        }
        {
            var Q0;
            Q0=makeQuery(id+"F9.opExtrude","CAP_EDGE",EDGE,{"disambiguationData":[OSD([sQuery(id+"F6.wireOp",EDGE,"E38")])],"isStart":true});
            var Q1;
            Q1=makeQuery(id+"F9.opExtrude","CAP_EDGE",EDGE,{"disambiguationData":[OSD([sQuery(id+"F6.wireOp",EDGE,"E26")])],"isStart":true});
            var Q2;
            Q2=makeQuery(id+"F9.opExtrude","CAP_EDGE",EDGE,{"disambiguationData":[OSD([sQuery(id+"F6.wireOp",EDGE,"E38")])],"isStart":false});
            var Q3;
            Q3=makeQuery(id+"F9.opExtrude","CAP_EDGE",EDGE,{"disambiguationData":[OSD([sQuery(id+"F6.wireOp",EDGE,"E26")])],"isStart":false});
            var Q4;
            Q4=makeQuery(id+"F10.opExtrude","CAP_FACE",FACE,{"disambiguationData":[OSD([sQuery(id+"F0.wireOp",EDGE,"E1"),sQuery(id+"F7.wireOp",EDGE,"E64"),sQuery(id+"F7.wireOp",EDGE,"E97")])],"isStart":true});
            var Q5;
            Q5=makeQuery(id+"F9.opExtrude","CAP_FACE",FACE,{"disambiguationData":[OSD([sQuery(id+"F0.wireOp",EDGE,"E1"),sQuery(id+"F6.wireOp",EDGE,"E25"),sQuery(id+"F6.wireOp",EDGE,"E37")])],"isStart":false});
            var Q6;
            Q6=makeQuery(id+"F9.opExtrude","CAP_FACE",FACE,{"disambiguationData":[OSD([sQuery(id+"F0.wireOp",EDGE,"E1"),sQuery(id+"F6.wireOp",EDGE,"E48"),sQuery(id+"F6.wireOp",EDGE,"E49")])],"isStart":false});
            var Q7;
            Q7=makeQuery(id+"F9.opExtrude","CAP_FACE",FACE,{"disambiguationData":[OSD([sQuery(id+"F0.wireOp",EDGE,"E1"),sQuery(id+"F6.wireOp",EDGE,"E27.MirrorCS"),sQuery(id+"F6.wireOp",EDGE,"E47.MirrorCS")])],"isStart":false});
            var Q8;
            Q8=makeQuery(id+"F9.opExtrude","CAP_FACE",FACE,{"disambiguationData":[OSD([sQuery(id+"F0.wireOp",EDGE,"E1"),sQuery(id+"F6.wireOp",EDGE,"E28.MirrorCS"),sQuery(id+"F6.wireOp",EDGE,"E46.MirrorCS")])],"isStart":false});
            var Q9;
            Q9=makeQuery(id+"F10.opExtrude","CAP_EDGE",EDGE,{"disambiguationData":[OSD([sQuery(id+"F7.wireOp",EDGE,"E65")])],"isStart":true});
            var Q10;
            Q10=makeQuery(id+"F10.opExtrude","CAP_FACE",FACE,{"disambiguationData":[OSD([sQuery(id+"F0.wireOp",EDGE,"E1"),sQuery(id+"F7.wireOp",EDGE,"E65"),sQuery(id+"F7.wireOp",EDGE,"E98")])],"isStart":true});
            var Q11;
            Q11=makeQuery(id+"F10.opExtrude","CAP_FACE",FACE,{"disambiguationData":[OSD([sQuery(id+"F0.wireOp",EDGE,"E1"),sQuery(id+"F7.wireOp",EDGE,"E66"),sQuery(id+"F7.wireOp",EDGE,"E99")])],"isStart":true});
            var Q12;
            Q12=makeQuery(id+"F9.opExtrude","CAP_FACE",FACE,{"disambiguationData":[OSD([sQuery(id+"F0.wireOp",EDGE,"E1"),sQuery(id+"F6.wireOp",EDGE,"E15"),sQuery(id+"F6.wireOp",EDGE,"E34")])],"isStart":false});
            var Q13;
            Q13=makeQuery(id+"F9.opExtrude","CAP_FACE",FACE,{"disambiguationData":[OSD([sQuery(id+"F0.wireOp",EDGE,"E1"),sQuery(id+"F6.wireOp",EDGE,"E16"),sQuery(id+"F6.wireOp",EDGE,"E35")])],"isStart":false});
            var Q14;
            Q14=makeQuery(id+"F9.opExtrude","CAP_EDGE",EDGE,{"disambiguationData":[OSD([sQuery(id+"F6.wireOp",EDGE,"E36")])],"isStart":false});
            var Q15;
            Q15=makeQuery(id+"F9.opExtrude","CAP_EDGE",EDGE,{"disambiguationData":[OSD([sQuery(id+"F6.wireOp",EDGE,"E24")])],"isStart":false});
            var Q16;
            Q16=makeQuery(id+"F9.opExtrude","CAP_EDGE",EDGE,{"disambiguationData":[OSD([sQuery(id+"F6.wireOp",EDGE,"E39.MirrorCS")])],"isStart":false});
            var Q17;
            Q17=makeQuery(id+"F9.opExtrude","CAP_EDGE",EDGE,{"disambiguationData":[OSD([sQuery(id+"F6.wireOp",EDGE,"E23.MirrorCS")])],"isStart":false});
            var Q18;
            Q18=makeQuery(id+"F9.opExtrude","CAP_EDGE",EDGE,{"disambiguationData":[OSD([sQuery(id+"F6.wireOp",EDGE,"E21.MirrorCS")])],"isStart":false});
            var Q19;
            Q19=makeQuery(id+"F9.opExtrude","CAP_EDGE",EDGE,{"disambiguationData":[OSD([sQuery(id+"F6.wireOp",EDGE,"E40.MirrorCS")])],"isStart":false});
            var Q20;
            Q20=makeQuery(id+"F9.opExtrude","CAP_EDGE",EDGE,{"disambiguationData":[OSD([sQuery(id+"F6.wireOp",EDGE,"E20.MirrorCS")])],"isStart":false});
            var Q21;
            Q21=makeQuery(id+"F9.opExtrude","CAP_FACE",FACE,{"disambiguationData":[OSD([sQuery(id+"F0.wireOp",EDGE,"E1"),sQuery(id+"F6.wireOp",EDGE,"E19.MirrorCS"),sQuery(id+"F6.wireOp",EDGE,"E42.MirrorCS")])],"isStart":false});
            var Q22;
            Q22=makeQuery(id+"F9.opExtrude","CAP_FACE",FACE,{"disambiguationData":[OSD([sQuery(id+"F0.wireOp",EDGE,"E1"),sQuery(id+"F6.wireOp",EDGE,"E18.MirrorCS"),sQuery(id+"F6.wireOp",EDGE,"E43.MirrorCS")])],"isStart":false});
            var Q23;
            Q23=makeQuery(id+"F9.opExtrude","CAP_FACE",FACE,{"disambiguationData":[OSD([sQuery(id+"F0.wireOp",EDGE,"E1"),sQuery(id+"F6.wireOp",EDGE,"E17.MirrorCS"),sQuery(id+"F6.wireOp",EDGE,"E44.MirrorCS")])],"isStart":false});
            var Q24;
            Q24=makeQuery(id+"F9.opExtrude","CAP_EDGE",EDGE,{"disambiguationData":[OSD([sQuery(id+"F6.wireOp",EDGE,"E29.MirrorCS")])],"isStart":false});
            var Q25;
            Q25=makeQuery(id+"F10.opExtrude","CAP_FACE",FACE,{"disambiguationData":[OSD([sQuery(id+"F0.wireOp",EDGE,"E1"),sQuery(id+"F7.wireOp",EDGE,"E60"),sQuery(id+"F7.wireOp",EDGE,"E93")])],"isStart":true});
            var Q26;
            Q26=makeQuery(id+"F10.opExtrude","CAP_EDGE",EDGE,{"disambiguationData":[OSD([sQuery(id+"F7.wireOp",EDGE,"E59")])],"isStart":true});
            var Q27;
            Q27=makeQuery(id+"F10.opExtrude","CAP_EDGE",EDGE,{"disambiguationData":[OSD([sQuery(id+"F7.wireOp",EDGE,"E92")])],"isStart":true});
            var Q28;
            Q28=makeQuery(id+"F10.opExtrude","CAP_EDGE",EDGE,{"disambiguationData":[OSD([sQuery(id+"F7.wireOp",EDGE,"E58")])],"isStart":true});
            var Q29;
            Q29=makeQuery(id+"F10.opExtrude","CAP_EDGE",EDGE,{"disambiguationData":[OSD([sQuery(id+"F7.wireOp",EDGE,"E91")])],"isStart":true});
            var Q30;
            Q30=makeQuery(id+"F10.opExtrude","CAP_EDGE",EDGE,{"disambiguationData":[OSD([sQuery(id+"F7.wireOp",EDGE,"E57")])],"isStart":true});
            var Q31;
            Q31=makeQuery(id+"F10.opExtrude","CAP_EDGE",EDGE,{"disambiguationData":[OSD([sQuery(id+"F7.wireOp",EDGE,"E55")])],"isStart":false});
            var Q32;
            Q32=makeQuery(id+"F10.opExtrude","CAP_EDGE",EDGE,{"disambiguationData":[OSD([sQuery(id+"F7.wireOp",EDGE,"E89")])],"isStart":true});
            var Q33;
            Q33=makeQuery(id+"F10.opExtrude","CAP_EDGE",EDGE,{"disambiguationData":[OSD([sQuery(id+"F7.wireOp",EDGE,"E88")])],"isStart":true});
            var Q34;
            Q34=makeQuery(id+"F10.opExtrude","CAP_EDGE",EDGE,{"disambiguationData":[OSD([sQuery(id+"F7.wireOp",EDGE,"E54")])],"isStart":true});
            var Q35;
            Q35=makeQuery(id+"F10.opExtrude","CAP_EDGE",EDGE,{"disambiguationData":[OSD([sQuery(id+"F7.wireOp",EDGE,"E61")])],"isStart":true});
            var Q36;
            Q36=makeQuery(id+"F10.opExtrude","CAP_EDGE",EDGE,{"disambiguationData":[OSD([sQuery(id+"F7.wireOp",EDGE,"E94")])],"isStart":true});
            var Q37;
            Q37=makeQuery(id+"F10.opExtrude","CAP_EDGE",EDGE,{"disambiguationData":[OSD([sQuery(id+"F7.wireOp",EDGE,"E62")])],"isStart":true});
            var Q38;
            Q38=makeQuery(id+"F10.opExtrude","CAP_EDGE",EDGE,{"disambiguationData":[OSD([sQuery(id+"F7.wireOp",EDGE,"E95")])],"isStart":true});
            var Q39;
            Q39=makeQuery(id+"F10.opExtrude","CAP_EDGE",EDGE,{"disambiguationData":[OSD([sQuery(id+"F7.wireOp",EDGE,"E53")])],"isStart":true});
            var Q40;
            Q40=makeQuery(id+"F10.opExtrude","CAP_EDGE",EDGE,{"disambiguationData":[OSD([sQuery(id+"F7.wireOp",EDGE,"E87")])],"isStart":true});
            var Q41;
            Q41=makeQuery(id+"F10.opExtrude","CAP_EDGE",EDGE,{"disambiguationData":[OSD([sQuery(id+"F7.wireOp",EDGE,"E117")])],"isStart":true});
            var Q42;
            Q42=makeQuery(id+"F10.opExtrude","CAP_EDGE",EDGE,{"disambiguationData":[OSD([sQuery(id+"F7.wireOp",EDGE,"E116")])],"isStart":true});
            var Q43;
            Q43=makeQuery(id+"F10.opExtrude","CAP_EDGE",EDGE,{"disambiguationData":[OSD([sQuery(id+"F7.wireOp",EDGE,"E86")])],"isStart":true});
            var Q44;
            Q44=makeQuery(id+"F10.opExtrude","CAP_EDGE",EDGE,{"disambiguationData":[OSD([sQuery(id+"F7.wireOp",EDGE,"E52")])],"isStart":true});
            var Q45;
            Q45=makeQuery(id+"F10.opExtrude","CAP_EDGE",EDGE,{"disambiguationData":[OSD([sQuery(id+"F7.wireOp",EDGE,"E51")])],"isStart":true});
            var Q46;
            Q46=makeQuery(id+"F10.opExtrude","CAP_EDGE",EDGE,{"disambiguationData":[OSD([sQuery(id+"F7.wireOp",EDGE,"E85")])],"isStart":true});
            var Q47;
            Q47=makeQuery(id+"F10.opExtrude","CAP_EDGE",EDGE,{"disambiguationData":[OSD([sQuery(id+"F7.wireOp",EDGE,"E50")])],"isStart":true});
            var Q48;
            Q48=makeQuery(id+"F10.opExtrude","CAP_EDGE",EDGE,{"disambiguationData":[OSD([sQuery(id+"F7.wireOp",EDGE,"E50")])],"isStart":true});
            var Q49;
            Q49=makeQuery(id+"F10.opExtrude","CAP_EDGE",EDGE,{"disambiguationData":[OSD([sQuery(id+"F7.wireOp",EDGE,"E84")])],"isStart":true});
            var Q50;
            Q50=makeQuery(id+"F10.opExtrude","CAP_EDGE",EDGE,{"disambiguationData":[OSD([sQuery(id+"F7.wireOp",EDGE,"E63")])],"isStart":true});
            var Q51;
            Q51=makeQuery(id+"F10.opExtrude","CAP_EDGE",EDGE,{"disambiguationData":[OSD([sQuery(id+"F7.wireOp",EDGE,"E96")])],"isStart":true});
            var Q52;
            Q52=makeQuery(id+"F10.opExtrude","CAP_EDGE",EDGE,{"disambiguationData":[OSD([sQuery(id+"F7.wireOp",EDGE,"E100.MirrorCS")])],"isStart":true});
            var Q53;
            Q53=makeQuery(id+"F10.opExtrude","CAP_EDGE",EDGE,{"disambiguationData":[OSD([sQuery(id+"F7.wireOp",EDGE,"E68.MirrorCS")])],"isStart":true});
            var Q54;
            Q54=makeQuery(id+"F9.opExtrude","CAP_EDGE",EDGE,{"disambiguationData":[OSD([sQuery(id+"F6.wireOp",EDGE,"E33")])],"isStart":false});
            var Q55;
            Q55=makeQuery(id+"F9.opExtrude","CAP_EDGE",EDGE,{"disambiguationData":[OSD([sQuery(id+"F6.wireOp",EDGE,"E14")])],"isStart":false});
            var Q56;
            Q56=makeQuery(id+"F9.opExtrude","CAP_EDGE",EDGE,{"disambiguationData":[OSD([sQuery(id+"F6.wireOp",EDGE,"E13")])],"isStart":false});
            var Q57;
            Q57=makeQuery(id+"F9.opExtrude","CAP_EDGE",EDGE,{"disambiguationData":[OSD([sQuery(id+"F6.wireOp",EDGE,"E32")])],"isStart":false});
            var Q58;
            Q58=makeQuery(id+"F9.opExtrude","CAP_EDGE",EDGE,{"disambiguationData":[OSD([sQuery(id+"F6.wireOp",EDGE,"E31")])],"isStart":false});
            var Q59;
            Q59=makeQuery(id+"F9.opExtrude","CAP_EDGE",EDGE,{"disambiguationData":[OSD([sQuery(id+"F6.wireOp",EDGE,"E12")])],"isStart":false});
            var Q60;
            Q60=makeQuery(id+"F9.opExtrude","CAP_EDGE",EDGE,{"disambiguationData":[OSD([sQuery(id+"F6.wireOp",EDGE,"E22")])],"isStart":false});
            var Q61;
            Q61=makeQuery(id+"F9.opExtrude","CAP_EDGE",EDGE,{"disambiguationData":[OSD([sQuery(id+"F6.wireOp",EDGE,"E30")])],"isStart":false});
            var Q62;
            Q62=makeQuery(id+"F10.opExtrude","CAP_EDGE",EDGE,{"disambiguationData":[OSD([sQuery(id+"F7.wireOp",EDGE,"E101.MirrorCS")])],"isStart":true});
            var Q63;
            Q63=makeQuery(id+"F10.opExtrude","CAP_EDGE",EDGE,{"disambiguationData":[OSD([sQuery(id+"F7.wireOp",EDGE,"E69.MirrorCS")])],"isStart":true});
            var Q64;
            Q64=makeQuery(id+"F10.opExtrude","CAP_EDGE",EDGE,{"disambiguationData":[OSD([sQuery(id+"F7.wireOp",EDGE,"E102.MirrorCS")])],"isStart":true});
            var Q65;
            Q65=makeQuery(id+"F10.opExtrude","CAP_EDGE",EDGE,{"disambiguationData":[OSD([sQuery(id+"F7.wireOp",EDGE,"E103.MirrorCS")])],"isStart":true});
            var Q66;
            Q66=makeQuery(id+"F10.opExtrude","CAP_EDGE",EDGE,{"disambiguationData":[OSD([sQuery(id+"F7.wireOp",EDGE,"E71.MirrorCS")])],"isStart":true});
            var Q67;
            Q67=makeQuery(id+"F10.opExtrude","CAP_EDGE",EDGE,{"disambiguationData":[OSD([sQuery(id+"F7.wireOp",EDGE,"E104.MirrorCS")])],"isStart":true});
            var Q68;
            Q68=makeQuery(id+"F10.opExtrude","CAP_EDGE",EDGE,{"disambiguationData":[OSD([sQuery(id+"F7.wireOp",EDGE,"E82.MirrorCS")])],"isStart":true});
            var Q69;
            Q69=makeQuery(id+"F10.opExtrude","CAP_EDGE",EDGE,{"disambiguationData":[OSD([sQuery(id+"F7.wireOp",EDGE,"E105.MirrorCS")])],"isStart":true});
            var Q70;
            Q70=makeQuery(id+"F10.opExtrude","CAP_EDGE",EDGE,{"disambiguationData":[OSD([sQuery(id+"F7.wireOp",EDGE,"E106.MirrorCS")])],"isStart":true});
            var Q71;
            Q71=makeQuery(id+"F10.opExtrude","CAP_EDGE",EDGE,{"disambiguationData":[OSD([sQuery(id+"F7.wireOp",EDGE,"E81.MirrorCS")])],"isStart":true});
            var Q72;
            Q72=makeQuery(id+"F10.opExtrude","CAP_EDGE",EDGE,{"disambiguationData":[OSD([sQuery(id+"F7.wireOp",EDGE,"E108.MirrorCS")])],"isStart":true});
            var Q73;
            Q73=makeQuery(id+"F10.opExtrude","CAP_EDGE",EDGE,{"disambiguationData":[OSD([sQuery(id+"F7.wireOp",EDGE,"E79.MirrorCS")])],"isStart":true});
            var Q74;
            Q74=makeQuery(id+"F9.opExtrude","CAP_EDGE",EDGE,{"disambiguationData":[OSD([sQuery(id+"F6.wireOp",EDGE,"E41.MirrorCS")])],"isStart":false});
            var Q75;
            Q75=makeQuery(id+"F10.opExtrude","CAP_EDGE",EDGE,{"disambiguationData":[OSD([sQuery(id+"F7.wireOp",EDGE,"E107.MirrorCS")])],"isStart":true});
            var Q76;
            Q76=makeQuery(id+"F10.opExtrude","CAP_EDGE",EDGE,{"disambiguationData":[OSD([sQuery(id+"F7.wireOp",EDGE,"E80.MirrorCS")])],"isStart":true});
            var Q77;
            Q77=makeQuery(id+"F10.opExtrude","CAP_EDGE",EDGE,{"disambiguationData":[OSD([sQuery(id+"F7.wireOp",EDGE,"E109.MirrorCS")])],"isStart":true});
            var Q78;
            Q78=makeQuery(id+"F10.opExtrude","CAP_EDGE",EDGE,{"disambiguationData":[OSD([sQuery(id+"F7.wireOp",EDGE,"E77.MirrorCS")])],"isStart":true});
            var Q79;
            Q79=makeQuery(id+"F10.opExtrude","CAP_EDGE",EDGE,{"disambiguationData":[OSD([sQuery(id+"F7.wireOp",EDGE,"E115.MirrorCS")])],"isStart":true});
            var Q80;
            Q80=makeQuery(id+"F10.opExtrude","CAP_FACE",FACE,{"disambiguationData":[OSD([sQuery(id+"F0.wireOp",EDGE,"E1"),sQuery(id+"F7.wireOp",EDGE,"E118.MirrorCS"),sQuery(id+"F7.wireOp",EDGE,"E119.MirrorCS")])],"isStart":true});
            var Q81;
            Q81=makeQuery(id+"F10.opExtrude","CAP_FACE",FACE,{"disambiguationData":[OSD([sQuery(id+"F0.wireOp",EDGE,"E1"),sQuery(id+"F7.wireOp",EDGE,"E75.MirrorCS"),sQuery(id+"F7.wireOp",EDGE,"E112.MirrorCS")])],"isStart":true});
            var Q82;
            Q82=makeQuery(id+"F10.opExtrude","CAP_EDGE",EDGE,{"disambiguationData":[OSD([sQuery(id+"F7.wireOp",EDGE,"E78.MirrorCS")])],"isStart":true});
            var Q83;
            Q83=makeQuery(id+"F9.opExtrude","CAP_EDGE",EDGE,{"disambiguationData":[OSD([sQuery(id+"F6.wireOp",EDGE,"E45.MirrorCS")])],"isStart":false});
            var Q84;
            Q84=makeQuery(id+"F10.opExtrude","CAP_EDGE",EDGE,{"disambiguationData":[OSD([sQuery(id+"F7.wireOp",EDGE,"E110.MirrorCS")])],"isStart":true});
            var Q85;
            Q85=makeQuery(id+"F10.opExtrude","CAP_EDGE",EDGE,{"disambiguationData":[OSD([sQuery(id+"F7.wireOp",EDGE,"E111.MirrorCS")])],"isStart":true});
            var Q86;
            Q86=makeQuery(id+"F10.opExtrude","CAP_EDGE",EDGE,{"disambiguationData":[OSD([sQuery(id+"F7.wireOp",EDGE,"E111.MirrorCS")])],"isStart":true});
            var Q87;
            Q87=makeQuery(id+"F10.opExtrude","CAP_EDGE",EDGE,{"disambiguationData":[OSD([sQuery(id+"F7.wireOp",EDGE,"E72.MirrorCS")])],"isStart":true});
            var Q88;
            Q88=makeQuery(id+"F10.opExtrude","CAP_FACE",FACE,{"disambiguationData":[OSD([sQuery(id+"F0.wireOp",EDGE,"E1"),sQuery(id+"F7.wireOp",EDGE,"E73.MirrorCS"),sQuery(id+"F7.wireOp",EDGE,"E114.MirrorCS")])],"isStart":true});
            var Q89;
            Q89=makeQuery(id+"F10.opExtrude","CAP_EDGE",EDGE,{"disambiguationData":[OSD([sQuery(id+"F7.wireOp",EDGE,"E73.MirrorCS")])],"isStart":true});
            var Q90;
            Q90=makeQuery(id+"F10.opExtrude","CAP_EDGE",EDGE,{"disambiguationData":[OSD([sQuery(id+"F7.wireOp",EDGE,"E74.MirrorCS")])],"isStart":true});
            var Q91;
            Q91=makeQuery(id+"F10.opExtrude","CAP_EDGE",EDGE,{"disambiguationData":[OSD([sQuery(id+"F7.wireOp",EDGE,"E113.MirrorCS")])],"isStart":true});
            var Q92;
            Q92=makeQuery(id+"F10.opExtrude","CAP_EDGE",EDGE,{"disambiguationData":[OSD([sQuery(id+"F7.wireOp",EDGE,"E76.MirrorCS")])],"isStart":true});
            var Q93;
            Q93=makeQuery(id+"F10.opExtrude","CAP_EDGE",EDGE,{"disambiguationData":[OSD([sQuery(id+"F7.wireOp",EDGE,"E83.MirrorCS")])],"isStart":true});
            var Q94;
            Q94=makeQuery(id+"F10.opExtrude","CAP_EDGE",EDGE,{"disambiguationData":[OSD([sQuery(id+"F7.wireOp",EDGE,"E90")])],"isStart":true});
            var Q95;
            Q95=makeQuery(id+"F10.opExtrude","CAP_EDGE",EDGE,{"disambiguationData":[OSD([sQuery(id+"F7.wireOp",EDGE,"E70.MirrorCS")])],"isStart":true});
            fillet(context, id + "F11", {"entities" : qUnion([Q0, Q1, Q2, Q3, Q4, Q5, Q6, Q7, Q8, Q9, Q10, Q11, Q12, Q13, Q14, Q15, Q16, Q17, Q18, Q19, Q20, Q21, Q22, Q23, Q24, Q25, Q26, Q27, Q28, Q29, Q30, Q31, Q32, Q33, Q34, Q35, Q36, Q37, Q38, Q39, Q40, Q41, Q42, Q43, Q44, Q45, Q46, Q47, Q48, Q49, Q50, Q51, Q52, Q53, Q54, Q55, Q56, Q57, Q58, Q59, Q60, Q61, Q62, Q63, Q64, Q65, Q66, Q67, Q68, Q69, Q70, Q71, Q72, Q73, Q74, Q75, Q76, Q77, Q78, Q79, Q80, Q81, Q82, Q83, Q84, Q85, Q86, Q87, Q88, Q89, Q90, Q91, Q92, Q93, Q94, Q95]), "radius" : 0.08 * mm, "tangentPropagation" : true, "allowEdgeOverflow" : false});
        }
        {
            var Q0;
            Q0=makeQuery(id+"F10.opExtrude","CAP_EDGE",EDGE,{"disambiguationData":[OSD([sQuery(id+"F7.wireOp",EDGE,"E66")])],"isStart":false});
            var Q1;
            Q1=makeQuery(id+"F10.opExtrude","CAP_EDGE",EDGE,{"disambiguationData":[OSD([sQuery(id+"F7.wireOp",EDGE,"E99")])],"isStart":false});
            var Q2;
            Q2=makeQuery(id+"F9.opExtrude","CAP_EDGE",EDGE,{"disambiguationData":[OSD([sQuery(id+"F6.wireOp",EDGE,"E14")])],"isStart":true});
            var Q3;
            Q3=makeQuery(id+"F9.opExtrude","CAP_EDGE",EDGE,{"disambiguationData":[OSD([sQuery(id+"F6.wireOp",EDGE,"E33")])],"isStart":true});
            var Q4;
            Q4=makeQuery(id+"F9.opExtrude","CAP_EDGE",EDGE,{"disambiguationData":[OSD([sQuery(id+"F6.wireOp",EDGE,"E30")])],"isStart":true});
            var Q5;
            Q5=makeQuery(id+"F10.opExtrude","CAP_EDGE",EDGE,{"disambiguationData":[OSD([sQuery(id+"F7.wireOp",EDGE,"E98")])],"isStart":false});
            var Q6;
            Q6=makeQuery(id+"F10.opExtrude","CAP_EDGE",EDGE,{"disambiguationData":[OSD([sQuery(id+"F7.wireOp",EDGE,"E65")])],"isStart":false});
            var Q7;
            Q7=makeQuery(id+"F10.opExtrude","CAP_EDGE",EDGE,{"disambiguationData":[OSD([sQuery(id+"F7.wireOp",EDGE,"E84")])],"isStart":false});
            var Q8;
            Q8=makeQuery(id+"F10.opExtrude","CAP_EDGE",EDGE,{"disambiguationData":[OSD([sQuery(id+"F7.wireOp",EDGE,"E50")])],"isStart":false});
            var Q9;
            {var subQ0=sQuery(id+"F7.wireOp",EDGE,"E51");Q9=makeQuery(id+"F11.opFillet","BLEND_EDGE",EDGE,{"blendedFrom":[makeQuery(id+"F10.opExtrude","CAP_EDGE",EDGE,{"disambiguationData":[OSD([subQ0])],"isStart":true}),makeQuery(id+"F10.opExtrude","SWEPT_FACE",FACE,{"disambiguationData":[OSD([subQ0])]})],"blendedInto":[makeQuery(id+"F10.opExtrude","SWEPT_FACE",FACE,{"disambiguationData":[OSD([subQ0])]})]});}
            var Q10;
            Q10=makeQuery(id+"F10.opExtrude","CAP_EDGE",EDGE,{"disambiguationData":[OSD([sQuery(id+"F7.wireOp",EDGE,"E85")])],"isStart":false});
            var Q11;
            Q11=makeQuery(id+"F9.opExtrude","CAP_EDGE",EDGE,{"disambiguationData":[OSD([sQuery(id+"F6.wireOp",EDGE,"E25")])],"isStart":true});
            var Q12;
            Q12=makeQuery(id+"F9.opExtrude","CAP_EDGE",EDGE,{"disambiguationData":[OSD([sQuery(id+"F6.wireOp",EDGE,"E37")])],"isStart":true});
            var Q13;
            {var subQ0=sQuery(id+"F6.wireOp",EDGE,"E26");Q13=makeQuery(id+"F11.opFillet","BLEND_EDGE",EDGE,{"blendedFrom":[makeQuery(id+"F9.opExtrude","CAP_EDGE",EDGE,{"disambiguationData":[OSD([subQ0])],"isStart":true}),makeQuery(id+"F9.opExtrude","CAP_FACE",FACE,{"disambiguationData":[OSD([sQuery(id+"F0.wireOp",EDGE,"E1"),subQ0,sQuery(id+"F6.wireOp",EDGE,"E38")])],"isStart":true})],"blendedInto":[makeQuery(id+"F9.opExtrude","CAP_FACE",FACE,{"disambiguationData":[OSD([sQuery(id+"F0.wireOp",EDGE,"E1"),subQ0,sQuery(id+"F6.wireOp",EDGE,"E38")])],"isStart":true})]});}
            var Q14;
            {var subQ0=sQuery(id+"F6.wireOp",EDGE,"E38");Q14=makeQuery(id+"F11.opFillet","BLEND_EDGE",EDGE,{"blendedFrom":[makeQuery(id+"F9.opExtrude","CAP_EDGE",EDGE,{"disambiguationData":[OSD([subQ0])],"isStart":true}),makeQuery(id+"F9.opExtrude","CAP_FACE",FACE,{"disambiguationData":[OSD([sQuery(id+"F0.wireOp",EDGE,"E1"),sQuery(id+"F6.wireOp",EDGE,"E26"),subQ0])],"isStart":true})],"blendedInto":[makeQuery(id+"F9.opExtrude","CAP_FACE",FACE,{"disambiguationData":[OSD([sQuery(id+"F0.wireOp",EDGE,"E1"),sQuery(id+"F6.wireOp",EDGE,"E26"),subQ0])],"isStart":true})]});}
            var Q15;
            Q15=makeQuery(id+"F9.opExtrude","CAP_EDGE",EDGE,{"disambiguationData":[OSD([sQuery(id+"F6.wireOp",EDGE,"E48")])],"isStart":true});
            var Q16;
            Q16=makeQuery(id+"F9.opExtrude","CAP_FACE",FACE,{"disambiguationData":[OSD([sQuery(id+"F0.wireOp",EDGE,"E1"),sQuery(id+"F6.wireOp",EDGE,"E27.MirrorCS"),sQuery(id+"F6.wireOp",EDGE,"E47.MirrorCS")])],"isStart":true});
            var Q17;
            Q17=makeQuery(id+"F9.opExtrude","CAP_FACE",FACE,{"disambiguationData":[OSD([sQuery(id+"F0.wireOp",EDGE,"E1"),sQuery(id+"F6.wireOp",EDGE,"E48"),sQuery(id+"F6.wireOp",EDGE,"E49")])],"isStart":true});
            var Q18;
            Q18=makeQuery(id+"F9.opExtrude","CAP_FACE",FACE,{"disambiguationData":[OSD([sQuery(id+"F0.wireOp",EDGE,"E1"),sQuery(id+"F6.wireOp",EDGE,"E28.MirrorCS"),sQuery(id+"F6.wireOp",EDGE,"E46.MirrorCS")])],"isStart":true});
            var Q19;
            Q19=makeQuery(id+"F9.opExtrude","CAP_EDGE",EDGE,{"disambiguationData":[OSD([sQuery(id+"F6.wireOp",EDGE,"E49")])],"isStart":true});
            var Q20;
            Q20=makeQuery(id+"F9.opExtrude","CAP_FACE",FACE,{"disambiguationData":[OSD([sQuery(id+"F0.wireOp",EDGE,"E1"),sQuery(id+"F6.wireOp",EDGE,"E29.MirrorCS"),sQuery(id+"F6.wireOp",EDGE,"E45.MirrorCS")])],"isStart":true});
            var Q21;
            Q21=makeQuery(id+"F9.opExtrude","CAP_FACE",FACE,{"disambiguationData":[OSD([sQuery(id+"F0.wireOp",EDGE,"E1"),sQuery(id+"F6.wireOp",EDGE,"E17.MirrorCS"),sQuery(id+"F6.wireOp",EDGE,"E44.MirrorCS")])],"isStart":true});
            var Q22;
            Q22=makeQuery(id+"F9.opExtrude","CAP_FACE",FACE,{"disambiguationData":[OSD([sQuery(id+"F0.wireOp",EDGE,"E1"),sQuery(id+"F6.wireOp",EDGE,"E24"),sQuery(id+"F6.wireOp",EDGE,"E36")])],"isStart":true});
            var Q23;
            Q23=makeQuery(id+"F9.opExtrude","CAP_FACE",FACE,{"disambiguationData":[OSD([sQuery(id+"F0.wireOp",EDGE,"E1"),sQuery(id+"F6.wireOp",EDGE,"E16"),sQuery(id+"F6.wireOp",EDGE,"E35")])],"isStart":true});
            var Q24;
            Q24=makeQuery(id+"F9.opExtrude","CAP_FACE",FACE,{"disambiguationData":[OSD([sQuery(id+"F0.wireOp",EDGE,"E1"),sQuery(id+"F6.wireOp",EDGE,"E15"),sQuery(id+"F6.wireOp",EDGE,"E34")])],"isStart":true});
            var Q25;
            Q25=makeQuery(id+"F10.opExtrude","CAP_FACE",FACE,{"disambiguationData":[OSD([sQuery(id+"F0.wireOp",EDGE,"E1"),sQuery(id+"F7.wireOp",EDGE,"E116"),sQuery(id+"F7.wireOp",EDGE,"E117")])],"isStart":false});
            var Q26;
            Q26=makeQuery(id+"F10.opExtrude","CAP_EDGE",EDGE,{"disambiguationData":[OSD([sQuery(id+"F7.wireOp",EDGE,"E53")])],"isStart":false});
            var Q27;
            Q27=makeQuery(id+"F10.opExtrude","CAP_EDGE",EDGE,{"disambiguationData":[OSD([sQuery(id+"F7.wireOp",EDGE,"E54")])],"isStart":false});
            var Q28;
            Q28=makeQuery(id+"F10.opExtrude","CAP_EDGE",EDGE,{"disambiguationData":[OSD([sQuery(id+"F7.wireOp",EDGE,"E88")])],"isStart":false});
            var Q29;
            Q29=makeQuery(id+"F9.opExtrude","CAP_FACE",FACE,{"disambiguationData":[OSD([sQuery(id+"F0.wireOp",EDGE,"E1"),sQuery(id+"F6.wireOp",EDGE,"E18.MirrorCS"),sQuery(id+"F6.wireOp",EDGE,"E43.MirrorCS")])],"isStart":true});
            var Q30;
            Q30=makeQuery(id+"F9.opExtrude","CAP_FACE",FACE,{"disambiguationData":[OSD([sQuery(id+"F0.wireOp",EDGE,"E1"),sQuery(id+"F6.wireOp",EDGE,"E19.MirrorCS"),sQuery(id+"F6.wireOp",EDGE,"E42.MirrorCS")])],"isStart":true});
            var Q31;
            Q31=makeQuery(id+"F9.opExtrude","CAP_FACE",FACE,{"disambiguationData":[OSD([sQuery(id+"F0.wireOp",EDGE,"E1"),sQuery(id+"F6.wireOp",EDGE,"E20.MirrorCS"),sQuery(id+"F6.wireOp",EDGE,"E41.MirrorCS")])],"isStart":true});
            var Q32;
            Q32=makeQuery(id+"F10.opExtrude","CAP_FACE",FACE,{"disambiguationData":[OSD([sQuery(id+"F0.wireOp",EDGE,"E1"),sQuery(id+"F7.wireOp",EDGE,"E55"),sQuery(id+"F7.wireOp",EDGE,"E89")])],"isStart":false});
            var Q33;
            Q33=makeQuery(id+"F10.opExtrude","CAP_FACE",FACE,{"disambiguationData":[OSD([sQuery(id+"F0.wireOp",EDGE,"E1"),sQuery(id+"F7.wireOp",EDGE,"E57"),sQuery(id+"F7.wireOp",EDGE,"E90")])],"isStart":false});
            var Q34;
            Q34=makeQuery(id+"F10.opExtrude","CAP_FACE",FACE,{"disambiguationData":[OSD([sQuery(id+"F0.wireOp",EDGE,"E1"),sQuery(id+"F7.wireOp",EDGE,"E58"),sQuery(id+"F7.wireOp",EDGE,"E91")])],"isStart":false});
            var Q35;
            Q35=makeQuery(id+"F10.opExtrude","CAP_FACE",FACE,{"disambiguationData":[OSD([sQuery(id+"F0.wireOp",EDGE,"E1"),sQuery(id+"F7.wireOp",EDGE,"E59"),sQuery(id+"F7.wireOp",EDGE,"E92")])],"isStart":false});
            var Q36;
            Q36=makeQuery(id+"F10.opExtrude","CAP_EDGE",EDGE,{"disambiguationData":[OSD([sQuery(id+"F7.wireOp",EDGE,"E52")])],"isStart":false});
            var Q37;
            Q37=makeQuery(id+"F10.opExtrude","CAP_EDGE",EDGE,{"disambiguationData":[OSD([sQuery(id+"F7.wireOp",EDGE,"E86")])],"isStart":false});
            var Q38;
            Q38=makeQuery(id+"F9.opExtrude","CAP_EDGE",EDGE,{"disambiguationData":[OSD([sQuery(id+"F6.wireOp",EDGE,"E12")])],"isStart":true});
            var Q39;
            Q39=makeQuery(id+"F9.opExtrude","CAP_EDGE",EDGE,{"disambiguationData":[OSD([sQuery(id+"F6.wireOp",EDGE,"E31")])],"isStart":true});
            var Q40;
            Q40=makeQuery(id+"F10.opExtrude","CAP_FACE",FACE,{"disambiguationData":[OSD([sQuery(id+"F0.wireOp",EDGE,"E1"),sQuery(id+"F7.wireOp",EDGE,"E68.MirrorCS"),sQuery(id+"F7.wireOp",EDGE,"E100.MirrorCS")])],"isStart":false});
            var Q41;
            Q41=makeQuery(id+"F10.opExtrude","CAP_FACE",FACE,{"disambiguationData":[OSD([sQuery(id+"F0.wireOp",EDGE,"E1"),sQuery(id+"F7.wireOp",EDGE,"E69.MirrorCS"),sQuery(id+"F7.wireOp",EDGE,"E101.MirrorCS")])],"isStart":false});
            var Q42;
            Q42=makeQuery(id+"F10.opExtrude","CAP_EDGE",EDGE,{"disambiguationData":[OSD([sQuery(id+"F7.wireOp",EDGE,"E102.MirrorCS")])],"isStart":false});
            var Q43;
            Q43=makeQuery(id+"F10.opExtrude","CAP_EDGE",EDGE,{"disambiguationData":[OSD([sQuery(id+"F7.wireOp",EDGE,"E70.MirrorCS")])],"isStart":false});
            var Q44;
            Q44=makeQuery(id+"F10.opExtrude","CAP_EDGE",EDGE,{"disambiguationData":[OSD([sQuery(id+"F7.wireOp",EDGE,"E71.MirrorCS")])],"isStart":false});
            var Q45;
            Q45=makeQuery(id+"F10.opExtrude","CAP_EDGE",EDGE,{"disambiguationData":[OSD([sQuery(id+"F7.wireOp",EDGE,"E103.MirrorCS")])],"isStart":false});
            var Q46;
            Q46=makeQuery(id+"F10.opExtrude","CAP_EDGE",EDGE,{"disambiguationData":[OSD([sQuery(id+"F7.wireOp",EDGE,"E83.MirrorCS")])],"isStart":false});
            var Q47;
            Q47=makeQuery(id+"F10.opExtrude","CAP_EDGE",EDGE,{"disambiguationData":[OSD([sQuery(id+"F7.wireOp",EDGE,"E82.MirrorCS")])],"isStart":false});
            var Q48;
            Q48=makeQuery(id+"F10.opExtrude","CAP_EDGE",EDGE,{"disambiguationData":[OSD([sQuery(id+"F7.wireOp",EDGE,"E105.MirrorCS")])],"isStart":false});
            var Q49;
            Q49=makeQuery(id+"F9.opExtrude","CAP_EDGE",EDGE,{"disambiguationData":[OSD([sQuery(id+"F6.wireOp",EDGE,"E13")])],"isStart":true});
            var Q50;
            Q50=makeQuery(id+"F9.opExtrude","CAP_EDGE",EDGE,{"disambiguationData":[OSD([sQuery(id+"F6.wireOp",EDGE,"E32")])],"isStart":true});
            var Q51;
            Q51=makeQuery(id+"F10.opExtrude","CAP_EDGE",EDGE,{"disambiguationData":[OSD([sQuery(id+"F7.wireOp",EDGE,"E81.MirrorCS")])],"isStart":false});
            var Q52;
            Q52=makeQuery(id+"F9.opExtrude","CAP_EDGE",EDGE,{"disambiguationData":[OSD([sQuery(id+"F6.wireOp",EDGE,"E40.MirrorCS")])],"isStart":true});
            var Q53;
            Q53=makeQuery(id+"F9.opExtrude","CAP_EDGE",EDGE,{"disambiguationData":[OSD([sQuery(id+"F6.wireOp",EDGE,"E39.MirrorCS")])],"isStart":true});
            var Q54;
            Q54=makeQuery(id+"F9.opExtrude","CAP_EDGE",EDGE,{"disambiguationData":[OSD([sQuery(id+"F6.wireOp",EDGE,"E23.MirrorCS")])],"isStart":true});
            var Q55;
            Q55=makeQuery(id+"F10.opExtrude","CAP_EDGE",EDGE,{"disambiguationData":[OSD([sQuery(id+"F7.wireOp",EDGE,"E104.MirrorCS")])],"isStart":false});
            var Q56;
            Q56=makeQuery(id+"F9.opExtrude","CAP_EDGE",EDGE,{"disambiguationData":[OSD([sQuery(id+"F6.wireOp",EDGE,"E21.MirrorCS")])],"isStart":true});
            var Q57;
            Q57=makeQuery(id+"F10.opExtrude","CAP_FACE",FACE,{"disambiguationData":[OSD([sQuery(id+"F0.wireOp",EDGE,"E1"),sQuery(id+"F7.wireOp",EDGE,"E81.MirrorCS"),sQuery(id+"F7.wireOp",EDGE,"E106.MirrorCS")])],"isStart":false});
            var Q58;
            Q58=makeQuery(id+"F10.opExtrude","CAP_FACE",FACE,{"disambiguationData":[OSD([sQuery(id+"F0.wireOp",EDGE,"E1"),sQuery(id+"F7.wireOp",EDGE,"E80.MirrorCS"),sQuery(id+"F7.wireOp",EDGE,"E107.MirrorCS")])],"isStart":false});
            var Q59;
            Q59=makeQuery(id+"F10.opExtrude","CAP_EDGE",EDGE,{"disambiguationData":[OSD([sQuery(id+"F7.wireOp",EDGE,"E93")])],"isStart":false});
            var Q60;
            Q60=makeQuery(id+"F10.opExtrude","CAP_EDGE",EDGE,{"disambiguationData":[OSD([sQuery(id+"F7.wireOp",EDGE,"E60")])],"isStart":false});
            var Q61;
            Q61=makeQuery(id+"F10.opExtrude","CAP_EDGE",EDGE,{"disambiguationData":[OSD([sQuery(id+"F7.wireOp",EDGE,"E94")])],"isStart":false});
            var Q62;
            Q62=makeQuery(id+"F10.opExtrude","CAP_EDGE",EDGE,{"disambiguationData":[OSD([sQuery(id+"F7.wireOp",EDGE,"E95")])],"isStart":false});
            var Q63;
            Q63=makeQuery(id+"F10.opExtrude","CAP_EDGE",EDGE,{"disambiguationData":[OSD([sQuery(id+"F7.wireOp",EDGE,"E62")])],"isStart":false});
            var Q64;
            Q64=makeQuery(id+"F10.opExtrude","CAP_EDGE",EDGE,{"disambiguationData":[OSD([sQuery(id+"F7.wireOp",EDGE,"E63")])],"isStart":false});
            var Q65;
            Q65=makeQuery(id+"F10.opExtrude","CAP_EDGE",EDGE,{"disambiguationData":[OSD([sQuery(id+"F7.wireOp",EDGE,"E96")])],"isStart":false});
            var Q66;
            Q66=makeQuery(id+"F10.opExtrude","CAP_EDGE",EDGE,{"disambiguationData":[OSD([sQuery(id+"F7.wireOp",EDGE,"E61")])],"isStart":false});
            var Q67;
            Q67=makeQuery(id+"F10.opExtrude","CAP_EDGE",EDGE,{"disambiguationData":[OSD([sQuery(id+"F7.wireOp",EDGE,"E64")])],"isStart":false});
            var Q68;
            Q68=makeQuery(id+"F10.opExtrude","CAP_EDGE",EDGE,{"disambiguationData":[OSD([sQuery(id+"F7.wireOp",EDGE,"E97")])],"isStart":false});
            var Q69;
            Q69=makeQuery(id+"F10.opExtrude","CAP_EDGE",EDGE,{"disambiguationData":[OSD([sQuery(id+"F7.wireOp",EDGE,"E79.MirrorCS")])],"isStart":false});
            var Q70;
            Q70=makeQuery(id+"F10.opExtrude","CAP_EDGE",EDGE,{"disambiguationData":[OSD([sQuery(id+"F7.wireOp",EDGE,"E108.MirrorCS")])],"isStart":false});
            var Q71;
            Q71=makeQuery(id+"F10.opExtrude","CAP_EDGE",EDGE,{"disambiguationData":[OSD([sQuery(id+"F7.wireOp",EDGE,"E72.MirrorCS")])],"isStart":false});
            var Q72;
            Q72=makeQuery(id+"F10.opExtrude","CAP_EDGE",EDGE,{"disambiguationData":[OSD([sQuery(id+"F7.wireOp",EDGE,"E114.MirrorCS")])],"isStart":false});
            var Q73;
            Q73=makeQuery(id+"F10.opExtrude","CAP_EDGE",EDGE,{"disambiguationData":[OSD([sQuery(id+"F7.wireOp",EDGE,"E73.MirrorCS")])],"isStart":false});
            var Q74;
            Q74=makeQuery(id+"F10.opExtrude","CAP_EDGE",EDGE,{"disambiguationData":[OSD([sQuery(id+"F7.wireOp",EDGE,"E115.MirrorCS")])],"isStart":false});
            var Q75;
            Q75=makeQuery(id+"F10.opExtrude","CAP_EDGE",EDGE,{"disambiguationData":[OSD([sQuery(id+"F7.wireOp",EDGE,"E74.MirrorCS")])],"isStart":false});
            var Q76;
            Q76=makeQuery(id+"F10.opExtrude","CAP_EDGE",EDGE,{"disambiguationData":[OSD([sQuery(id+"F7.wireOp",EDGE,"E113.MirrorCS")])],"isStart":false});
            var Q77;
            Q77=makeQuery(id+"F10.opExtrude","CAP_FACE",FACE,{"disambiguationData":[OSD([sQuery(id+"F0.wireOp",EDGE,"E1"),sQuery(id+"F7.wireOp",EDGE,"E118.MirrorCS"),sQuery(id+"F7.wireOp",EDGE,"E119.MirrorCS")])],"isStart":false});
            var Q78;
            Q78=makeQuery(id+"F10.opExtrude","CAP_EDGE",EDGE,{"disambiguationData":[OSD([sQuery(id+"F7.wireOp",EDGE,"E112.MirrorCS")])],"isStart":false});
            var Q79;
            Q79=makeQuery(id+"F10.opExtrude","CAP_EDGE",EDGE,{"disambiguationData":[OSD([sQuery(id+"F7.wireOp",EDGE,"E111.MirrorCS")])],"isStart":false});
            var Q80;
            Q80=makeQuery(id+"F10.opExtrude","CAP_EDGE",EDGE,{"disambiguationData":[OSD([sQuery(id+"F7.wireOp",EDGE,"E76.MirrorCS")])],"isStart":false});
            var Q81;
            Q81=makeQuery(id+"F10.opExtrude","CAP_EDGE",EDGE,{"disambiguationData":[OSD([sQuery(id+"F7.wireOp",EDGE,"E75.MirrorCS")])],"isStart":false});
            var Q82;
            Q82=makeQuery(id+"F10.opExtrude","CAP_EDGE",EDGE,{"disambiguationData":[OSD([sQuery(id+"F7.wireOp",EDGE,"E109.MirrorCS")])],"isStart":false});
            var Q83;
            Q83=makeQuery(id+"F10.opExtrude","CAP_EDGE",EDGE,{"disambiguationData":[OSD([sQuery(id+"F7.wireOp",EDGE,"E78.MirrorCS")])],"isStart":false});
            var Q84;
            Q84=makeQuery(id+"F10.opExtrude","CAP_EDGE",EDGE,{"disambiguationData":[OSD([sQuery(id+"F7.wireOp",EDGE,"E110.MirrorCS")])],"isStart":false});
            var Q85;
            Q85=makeQuery(id+"F10.opExtrude","CAP_EDGE",EDGE,{"disambiguationData":[OSD([sQuery(id+"F7.wireOp",EDGE,"E77.MirrorCS")])],"isStart":false});
            fillet(context, id + "F12", {"entities" : qUnion([Q0, Q1, Q2, Q3, Q4, Q5, Q6, Q7, Q8, Q9, Q10, Q11, Q12, Q13, Q14, Q15, Q16, Q17, Q18, Q19, Q20, Q21, Q22, Q23, Q24, Q25, Q26, Q27, Q28, Q29, Q30, Q31, Q32, Q33, Q34, Q35, Q36, Q37, Q38, Q39, Q40, Q41, Q42, Q43, Q44, Q45, Q46, Q47, Q48, Q49, Q50, Q51, Q52, Q53, Q54, Q55, Q56, Q57, Q58, Q59, Q60, Q61, Q62, Q63, Q64, Q65, Q66, Q67, Q68, Q69, Q70, Q71, Q72, Q73, Q74, Q75, Q76, Q77, Q78, Q79, Q80, Q81, Q82, Q83, Q84, Q85]), "radius" : 0.08 * mm, "tangentPropagation" : true, "allowEdgeOverflow" : false});
        }
        {
            var Q0;
            Q0=makeQuery(id+"F1.opExtrude","SWEPT_FACE",FACE,{"disambiguationData":[OSD([sQuery(id+"F0.wireOp",EDGE,"E0")])]});
            var Q1;
            Q1=makeQuery(id+"F1.opExtrude","CAP_EDGE",EDGE,{"disambiguationData":[OSD([sQuery(id+"F0.wireOp",EDGE,"E1")])],"isStart":false});
            fillet(context, id + "F13", {"entities" : qUnion([Q0, Q1]), "radius" : 0.25 * mm, "tangentPropagation" : true, "allowEdgeOverflow" : false});
        }
        {
            var Q0;
            Q0=makeQuery(id+"F3.boolean.opBoolean","COPY",EDGE,{"derivedFrom":makeQuery(id+"F3.opExtrude","CAP_EDGE",EDGE,{"disambiguationData":[OSD([sQuery(id+"F2.wireOp",EDGE,"E6")])],"isStart":true})});
            var Q1;
            Q1=makeQuery(id+"F3.boolean.opBoolean","INTERSECT",EDGE,{"derivedFrom":[makeQuery(id+"F1.opExtrude","CAP_FACE",FACE,{"disambiguationData":[OSD([sQuery(id+"F0.wireOp",EDGE,"E0"),sQuery(id+"F0.wireOp",EDGE,"E1"),sQuery(id+"F0.wireOp",EDGE,"E2"),sQuery(id+"F0.wireOp",EDGE,"E3.MirrorCS")])],"isStart":true}),makeQuery(id+"F3.opExtrude","SWEPT_FACE",FACE,{"disambiguationData":[OSD([sQuery(id+"F2.wireOp",EDGE,"E6")])]})]});
            var Q2;
            Q2=makeQuery(id+"F3.boolean.opBoolean","INTERSECT",EDGE,{"derivedFrom":[makeQuery(id+"F1.opExtrude","CAP_FACE",FACE,{"disambiguationData":[OSD([sQuery(id+"F0.wireOp",EDGE,"E0"),sQuery(id+"F0.wireOp",EDGE,"E1"),sQuery(id+"F0.wireOp",EDGE,"E2"),sQuery(id+"F0.wireOp",EDGE,"E3.MirrorCS")])],"isStart":true}),makeQuery(id+"F3.opExtrude","SWEPT_FACE",FACE,{"disambiguationData":[OSD([sQuery(id+"F2.wireOp",EDGE,"E5")])]})]});
            var Q3;
            Q3=makeQuery(id+"F3.boolean.opBoolean","COPY",EDGE,{"derivedFrom":makeQuery(id+"F3.opExtrude","CAP_EDGE",EDGE,{"disambiguationData":[OSD([sQuery(id+"F2.wireOp",EDGE,"E5")])],"isStart":true})});
            var Q4;
            Q4=makeQuery(id+"F3.boolean.opBoolean","INTERSECT",EDGE,{"derivedFrom":[makeQuery(id+"F1.opExtrude","CAP_FACE",FACE,{"disambiguationData":[OSD([sQuery(id+"F0.wireOp",EDGE,"E0"),sQuery(id+"F0.wireOp",EDGE,"E1"),sQuery(id+"F0.wireOp",EDGE,"E2"),sQuery(id+"F0.wireOp",EDGE,"E3.MirrorCS")])],"isStart":true}),makeQuery(id+"F3.opExtrude","SWEPT_FACE",FACE,{"disambiguationData":[OSD([sQuery(id+"F2.wireOp",EDGE,"E4")])]})]});
            var Q5;
            Q5=makeQuery(id+"F3.boolean.opBoolean","COPY",EDGE,{"derivedFrom":makeQuery(id+"F3.opExtrude","CAP_EDGE",EDGE,{"disambiguationData":[OSD([sQuery(id+"F2.wireOp",EDGE,"E4")])],"isStart":true})});
            fillet(context, id + "F14", {"entities" : qUnion([Q0, Q1, Q2, Q3, Q4, Q5]), "radius" : 0.2 * mm, "tangentPropagation" : true, "allowEdgeOverflow" : false});
        }
    });
